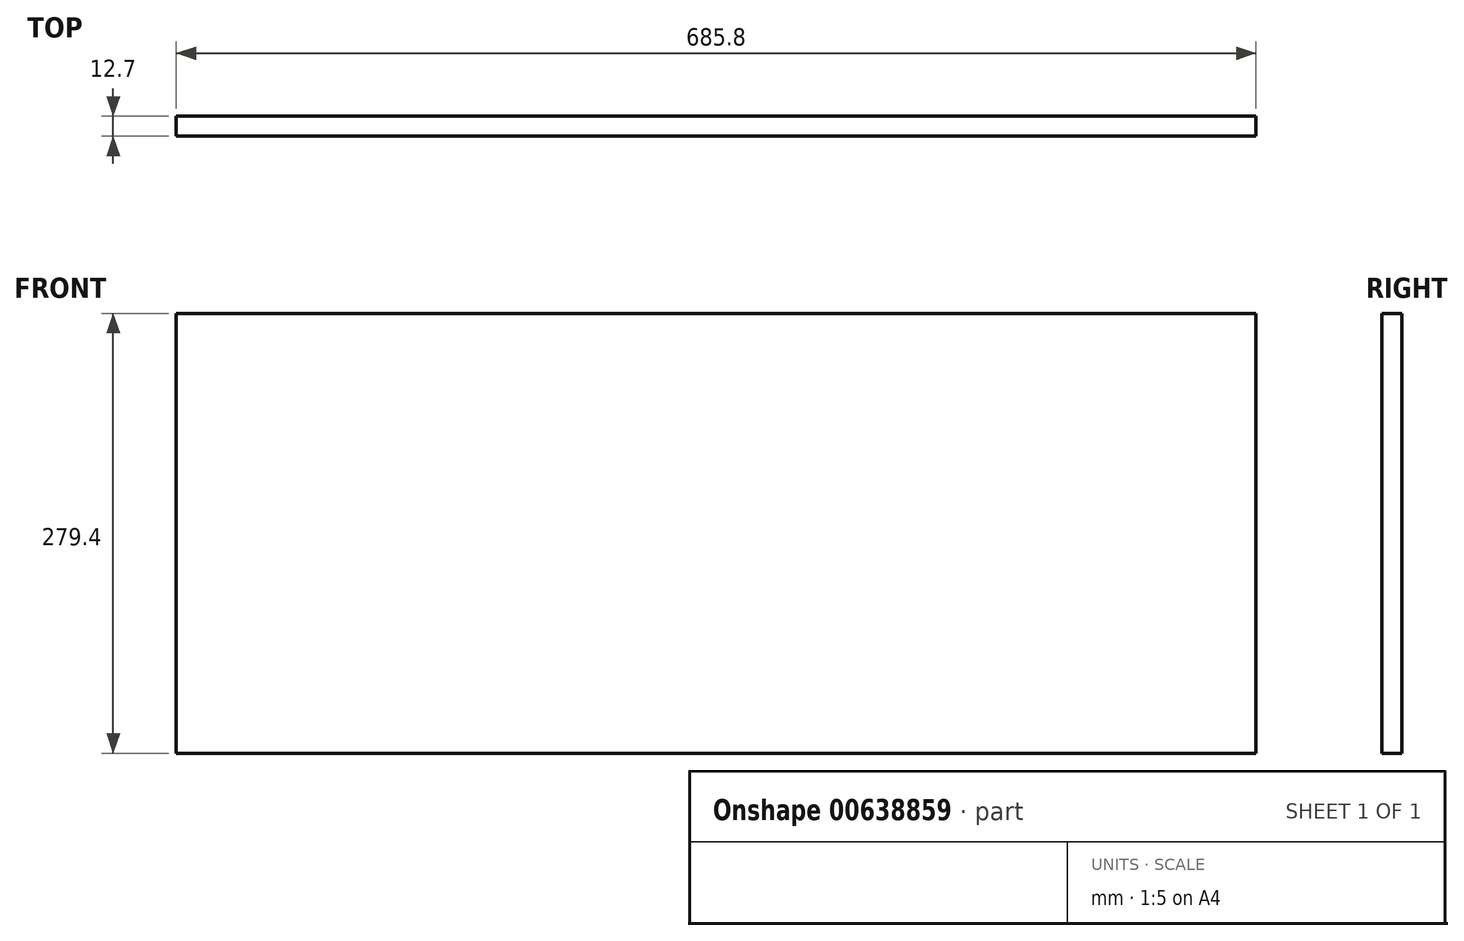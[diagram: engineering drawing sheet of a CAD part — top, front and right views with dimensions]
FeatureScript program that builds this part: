
annotation { "Feature Type Name" : "Feature", "Feature Type Description" : "" }
export const myFeature = defineFeature(function(context is Context, id is Id, definition is map)
    precondition{}
    {
        {
            var Q0;
            Q0=qCreatedBy(makeId("Front.planeOp"),FACE);
            var sketch = newSketch(context, id + "F0", { "sketchPlane" : qUnion([Q0])});
            skLineSegment(sketch, "E0.bottom", {"start": v(342.9, 139.7) * mm, "end": v(-342.9, 139.7) * mm});
            skLineSegment(sketch, "E0.top", {"start": v(342.9, -139.7) * mm, "end": v(-342.9, -139.7) * mm});
            skLineSegment(sketch, "E0.left", {"start": v(342.9, 139.7) * mm, "end": v(342.9, -139.7) * mm});
            skLineSegment(sketch, "E0.right", {"start": v(-342.9, 139.7) * mm, "end": v(-342.9, -139.7) * mm});
            skPoint(sketch, "E0.middle", {"position": v(0, 0) * mm});
            skSolve(sketch);
        }
        {
            var Q0;
            Q0=makeQuery(id+"F0.imprint","IMPRINT",FACE,{"disambiguationData":[TD([[makeQuery(id+"F0.imprint","IMPRINT",EDGE,{"derivedFrom":sQuery(id+"F0.wireOp",EDGE,"E0.bottom")}),1.0]])]});
            extrude(context, id + "F1", {"entities" : qUnion([Q0]), "depth" : 12.7 * mm, "offsetDistance" : 25.4 * mm});
        }
    });
